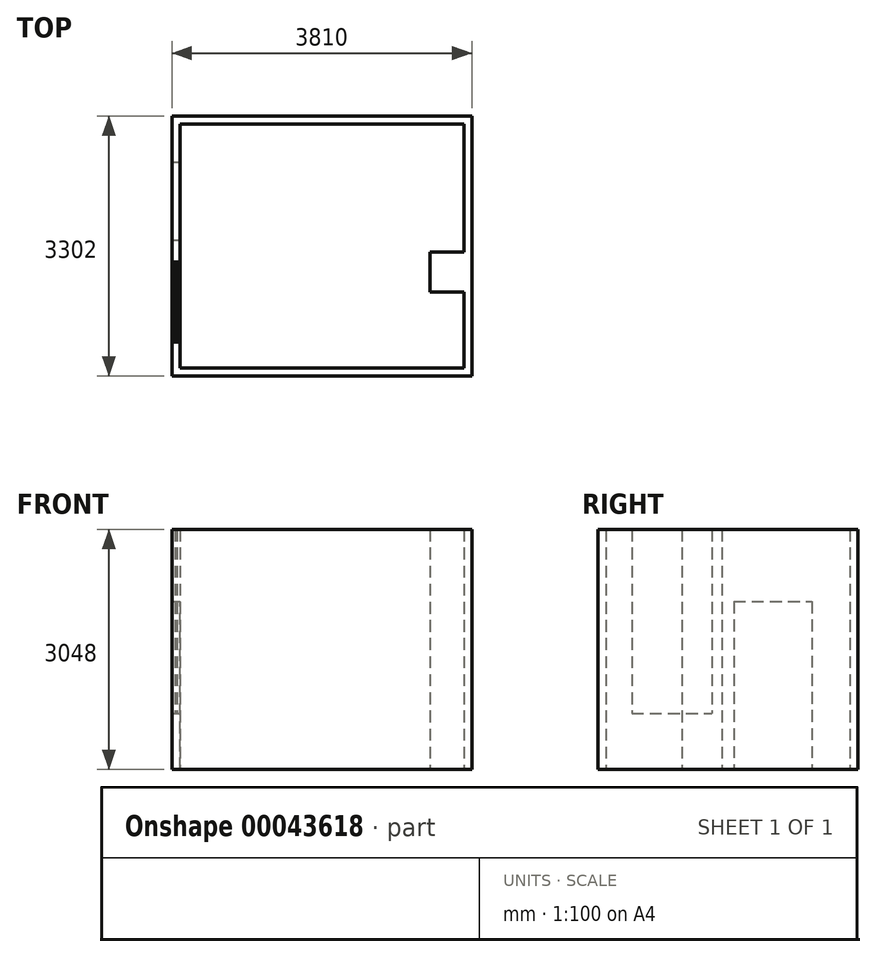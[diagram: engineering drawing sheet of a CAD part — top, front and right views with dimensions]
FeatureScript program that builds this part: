
annotation { "Feature Type Name" : "Feature", "Feature Type Description" : "" }
export const myFeature = defineFeature(function(context is Context, id is Id, definition is map)
    precondition{}
    {
        {
            var Q0;
            Q0=qCreatedBy(makeId("Top.planeOp"),FACE);
            var sketch = newSketch(context, id + "F0", { "sketchPlane" : qUnion([Q0])});
            skLineSegment(sketch, "E0.bottom", {"start": v(-1803.4, 1549.4) * mm, "end": v(1803.4, 1549.4) * mm});
            skLineSegment(sketch, "E0.top", {"start": v(-1803.4, -1549.4) * mm, "end": v(1803.4, -1549.4) * mm});
            skLineSegment(sketch, "E0.left", {"start": v(-1803.4, 1549.4) * mm, "end": v(-1803.4, -1549.4) * mm});
            skLineSegment(sketch, "E0.right", {"start": v(1803.4, 1549.4) * mm, "end": v(1803.4, -1549.4) * mm});
            skLineSegment(sketch, "E1.0", {"start": v(-1905, 1651) * mm, "end": v(1905, 1651) * mm});
            skLineSegment(sketch, "E1.1", {"start": v(-1905, 1651) * mm, "end": v(-1905, -1651) * mm});
            skLineSegment(sketch, "E1.2", {"start": v(-1905, -1651) * mm, "end": v(1905, -1651) * mm});
            skLineSegment(sketch, "E1.3", {"start": v(1905, 1651) * mm, "end": v(1905, -1651) * mm});
            skSolve(sketch);
        }
        {
            var Q0;
            Q0=makeQuery(id+"F0.imprint","IMPRINT",FACE,{"disambiguationData":[TD([[makeQuery(id+"F0.imprint","IMPRINT",EDGE,{"derivedFrom":sQuery(id+"F0.wireOp",EDGE,"E0.bottom")}),1.0]])]});
            extrude(context, id + "F1", {"entities" : qUnion([Q0]), "depth" : 3048 * mm});
        }
        {
            var Q0;
            Q0=makeQuery(id+"F1.opExtrude","SWEPT_FACE",FACE,{"disambiguationData":[OSD([sQuery(id+"F0.wireOp",EDGE,"E0.left")])]});
            var sketch = newSketch(context, id + "F2", { "sketchPlane" : qUnion([Q0])});
            skLineSegment(sketch, "E2.bottom", {"start": v(1066.8, 0) * mm, "end": v(76.2, 0) * mm});
            skLineSegment(sketch, "E2.top", {"start": v(1066.8, 2133.6) * mm, "end": v(76.2, 2133.6) * mm});
            skLineSegment(sketch, "E2.left", {"start": v(1066.8, 0) * mm, "end": v(1066.8, 2133.6) * mm});
            skLineSegment(sketch, "E2.right", {"start": v(76.2, 0) * mm, "end": v(76.2, 2133.6) * mm});
            skSolve(sketch);
        }
        {
            var Q0;
            Q0 = qSketchRegion(id + "F2", true);
            extrude(context, id + "F3", {"entities" : qUnion([Q0]), "operationType" : NewBodyOperationType.REMOVE, "endBound" : BoundingType.UP_TO_NEXT, "oppositeDirection" : true, "depth" : 25.4 * mm});
        }
        {
            var Q0;
            Q0=makeQuery(id+"F1.opExtrude","CAP_FACE",FACE,{"disambiguationData":[OSD([sQuery(id+"F0.wireOp",EDGE,"E0.bottom"),sQuery(id+"F0.wireOp",EDGE,"E0.top"),sQuery(id+"F0.wireOp",EDGE,"E0.left"),sQuery(id+"F0.wireOp",EDGE,"E0.right"),sQuery(id+"F0.wireOp",EDGE,"E1.0"),sQuery(id+"F0.wireOp",EDGE,"E1.1"),sQuery(id+"F0.wireOp",EDGE,"E1.2"),sQuery(id+"F0.wireOp",EDGE,"E1.3")])],"isStart":true});
            var sketch = newSketch(context, id + "F4", { "sketchPlane" : qUnion([Q0])});
            skLineSegment(sketch, "E3.bottom", {"start": v(1803.4, 584.2) * mm, "end": v(1371.6, 584.2) * mm});
            skLineSegment(sketch, "E3.top", {"start": v(1803.4, 76.2) * mm, "end": v(1371.6, 76.2) * mm});
            skLineSegment(sketch, "E3.left", {"start": v(1803.4, 584.2) * mm, "end": v(1803.4, 76.2) * mm});
            skLineSegment(sketch, "E3.right", {"start": v(1371.6, 584.2) * mm, "end": v(1371.6, 76.2) * mm});
            skSolve(sketch);
        }
        {
            var Q0;
            Q0 = qSketchRegion(id + "F4", true);
            var Q1;
            Q1=makeQuery(id+"F1.opExtrude","CAP_FACE",FACE,{"disambiguationData":[OSD([sQuery(id+"F0.wireOp",EDGE,"E0.bottom"),sQuery(id+"F0.wireOp",EDGE,"E0.top"),sQuery(id+"F0.wireOp",EDGE,"E0.left"),sQuery(id+"F0.wireOp",EDGE,"E0.right"),sQuery(id+"F0.wireOp",EDGE,"E1.0"),sQuery(id+"F0.wireOp",EDGE,"E1.1"),sQuery(id+"F0.wireOp",EDGE,"E1.2"),sQuery(id+"F0.wireOp",EDGE,"E1.3")])],"isStart":false});
            extrude(context, id + "F5", {"entities" : qUnion([Q0]), "operationType" : NewBodyOperationType.ADD, "endBound" : BoundingType.UP_TO_SURFACE, "oppositeDirection" : true, "endBoundEntityFace" : qUnion([Q1]), "depth" : 25.4 * mm});
        }
        {
            var Q0;
            Q0=makeQuery(id+"F1.opExtrude","SWEPT_FACE",FACE,{"disambiguationData":[OSD([sQuery(id+"F0.wireOp",EDGE,"E0.left")])]});
            var sketch = newSketch(context, id + "F6", { "sketchPlane" : qUnion([Q0])});
            skLineSegment(sketch, "E4.bottom", {"start": v(-1219.2, 3048) * mm, "end": v(-203.2, 3048) * mm});
            skLineSegment(sketch, "E4.top", {"start": v(-1219.2, 711.2) * mm, "end": v(-203.2, 711.2) * mm});
            skLineSegment(sketch, "E4.left", {"start": v(-1219.2, 3048) * mm, "end": v(-1219.2, 711.2) * mm});
            skLineSegment(sketch, "E4.right", {"start": v(-203.2, 3048) * mm, "end": v(-203.2, 711.2) * mm});
            skSolve(sketch);
        }
        {
            var Q0;
            Q0 = qSketchRegion(id + "F6", true);
            extrude(context, id + "F7", {"entities" : qUnion([Q0]), "operationType" : NewBodyOperationType.REMOVE, "endBound" : BoundingType.UP_TO_NEXT, "oppositeDirection" : true, "depth" : 25.4 * mm});
        }
        {
            var Q0;
            Q0=makeQuery(id+"F7.boolean.opBoolean","COPY",FACE,{"derivedFrom":makeQuery(id+"F7.opExtrude","SWEPT_FACE",FACE,{"disambiguationData":[OSD([sQuery(id+"F6.wireOp",EDGE,"E4.top")])]})});
            var sketch = newSketch(context, id + "F8", { "sketchPlane" : qUnion([Q0])});
            skLineSegment(sketch, "E5.bottom", {"start": v(-1866.9, -1219.2) * mm, "end": v(-1841.5, -1219.2) * mm});
            skLineSegment(sketch, "E5.top", {"start": v(-1866.9, -203.2) * mm, "end": v(-1841.5, -203.2) * mm});
            skLineSegment(sketch, "E5.left", {"start": v(-1866.9, -1219.2) * mm, "end": v(-1866.9, -203.2) * mm});
            skLineSegment(sketch, "E5.right", {"start": v(-1841.5, -1219.2) * mm, "end": v(-1841.5, -203.2) * mm});
            skSolve(sketch);
        }
        {
            var Q0;
            Q0 = qSketchRegion(id + "F8", true);
            var Q1;
            Q1=makeQuery(id+"F5.boolean.opBoolean","MERGE",FACE,{"derivedFrom":[makeQuery(id+"F1.opExtrude","CAP_FACE",FACE,{"disambiguationData":[OSD([sQuery(id+"F0.wireOp",EDGE,"E0.bottom"),sQuery(id+"F0.wireOp",EDGE,"E0.top"),sQuery(id+"F0.wireOp",EDGE,"E0.left"),sQuery(id+"F0.wireOp",EDGE,"E0.right"),sQuery(id+"F0.wireOp",EDGE,"E1.0"),sQuery(id+"F0.wireOp",EDGE,"E1.1"),sQuery(id+"F0.wireOp",EDGE,"E1.2"),sQuery(id+"F0.wireOp",EDGE,"E1.3")])],"isStart":false}),makeQuery(id+"F5.opExtrude","CAP_FACE",FACE,{"disambiguationData":[OSD([sQuery(id+"F4.wireOp",EDGE,"E3.bottom"),sQuery(id+"F4.wireOp",EDGE,"E3.top"),sQuery(id+"F4.wireOp",EDGE,"E3.left"),sQuery(id+"F4.wireOp",EDGE,"E3.right")])],"isStart":false})]});
            extrude(context, id + "F9", {"entities" : qUnion([Q0]), "endBound" : BoundingType.UP_TO_SURFACE, "endBoundEntityFace" : qUnion([Q1]), "depth" : 25.4 * mm});
        }
    });
